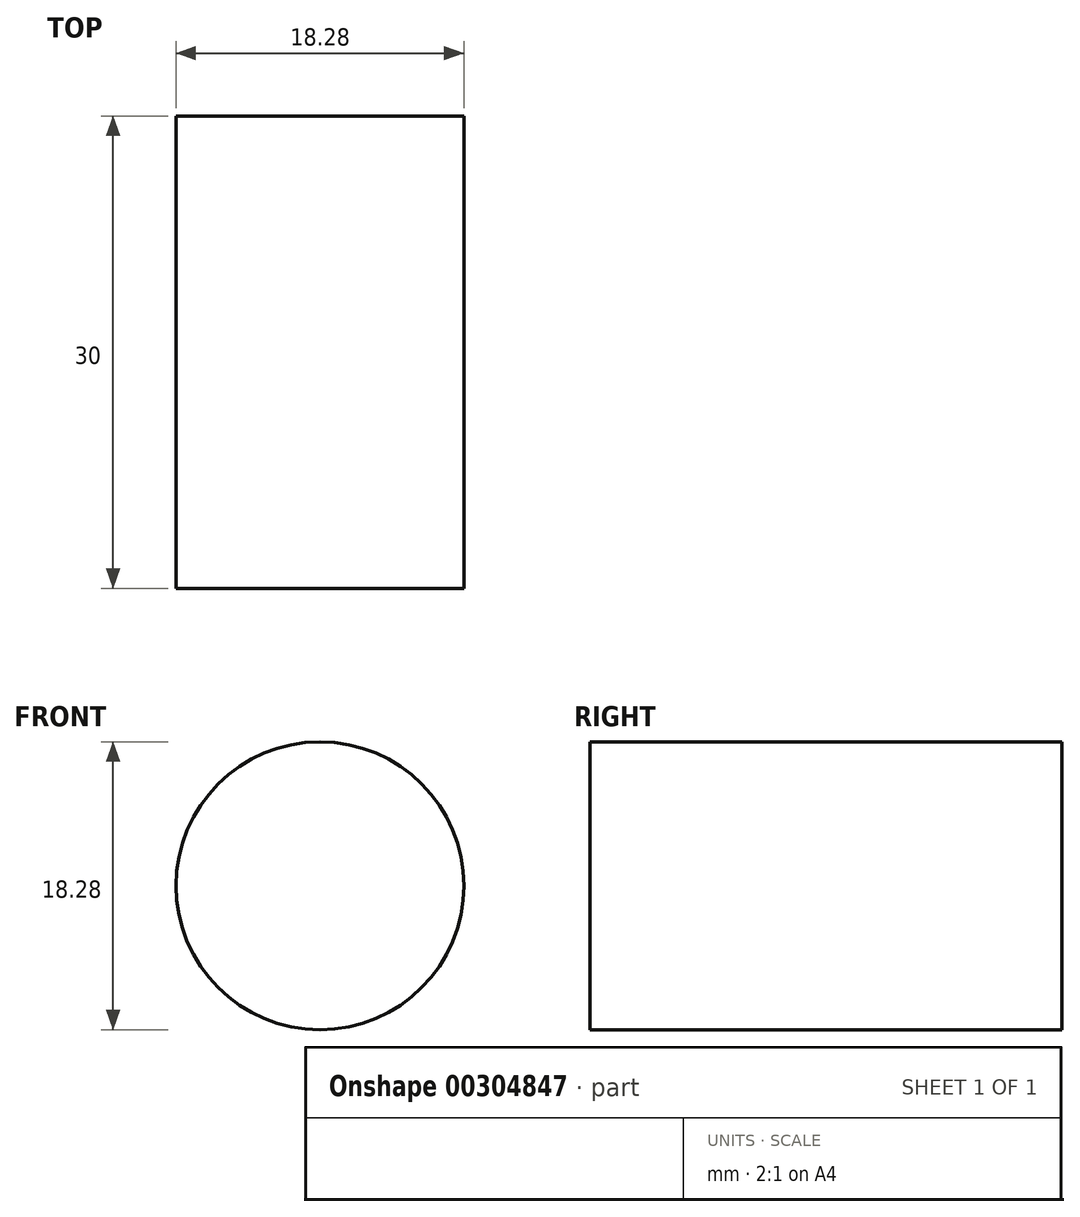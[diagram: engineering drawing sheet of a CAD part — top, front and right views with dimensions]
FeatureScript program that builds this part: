
annotation { "Feature Type Name" : "Feature", "Feature Type Description" : "" }
export const myFeature = defineFeature(function(context is Context, id is Id, definition is map)
    precondition{}
    {
        {
            var Q0;
            Q0=qCreatedBy(makeId("Front.planeOp"),FACE);
            var sketch = newSketch(context, id + "F0", { "sketchPlane" : qUnion([Q0])});
            skPoint(sketch, "E0", {"position": v(9.14, 0) * mm});
            skCircle(sketch, "E1", {"center": v(0, 0) * mm, "radius": 9.14 * mm});
            skSolve(sketch);
        }
        {
            var Q0;
            Q0=makeQuery(id+"F0.imprint","IMPRINT",FACE,{"disambiguationData":[TD([[makeQuery(id+"F0.imprint","IMPRINT",EDGE,{"derivedFrom":sQuery(id+"F0.wireOp",EDGE,"E1")}),1.0]])]});
            extrude(context, id + "F1", {"entities" : qUnion([Q0]), "depth" : 30 * mm});
        }
    });
